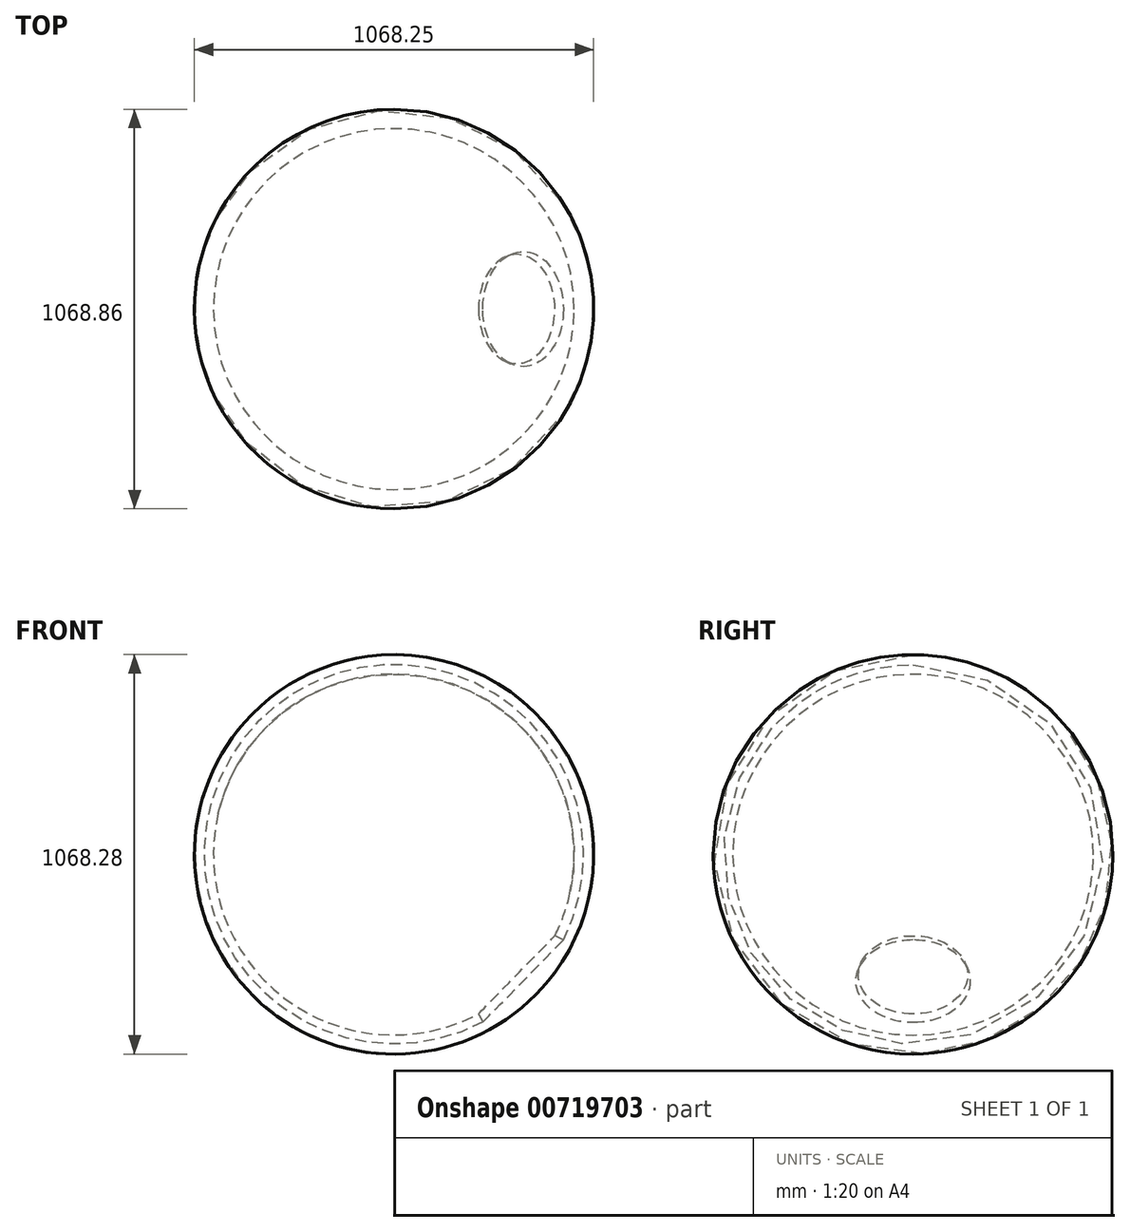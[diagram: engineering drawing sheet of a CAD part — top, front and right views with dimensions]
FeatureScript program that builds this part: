
annotation { "Feature Type Name" : "Feature", "Feature Type Description" : "" }
export const myFeature = defineFeature(function(context is Context, id is Id, definition is map)
    precondition{}
    {
        {
            var Q0;
            Q0=qCreatedBy(makeId("Front.planeOp"),FACE);
            var sketch = newSketch(context, id + "F0", { "sketchPlane" : qUnion([Q0])});
            skArc(sketch, "E0", {"start": v(469.78, -110.48) * mm, "mid": v(110.48, 469.78) * mm, "end": v(-469.78, 110.48) * mm});
            skLineSegment(sketch, "E1", {"start": v(469.78, -110.48) * mm, "end": v(0, 0) * mm});
            skLineSegment(sketch, "E2", {"start": v(0, 0) * mm, "end": v(-469.78, 110.48) * mm});
            skSolve(sketch);
        }
        {
            var Q0;
            Q0=makeQuery(id+"F0.imprint","IMPRINT",FACE,{"disambiguationData":[TD([[makeQuery(id+"F0.imprint","IMPRINT",EDGE,{"derivedFrom":sQuery(id+"F0.wireOp",EDGE,"E0")}),1.0]])]});
            var sketch = newSketch(context, id + "F1", { "sketchPlane" : qUnion([Q0])});
            skArc(sketch, "E3", {"start": v(453.81, -228.3) * mm, "mid": v(228.3, 453.81) * mm, "end": v(-453.81, 228.3) * mm});
            skLineSegment(sketch, "E4", {"start": v(0, 0) * mm, "end": v(453.81, -228.3) * mm});
            skLineSegment(sketch, "E5", {"start": v(453.81, -228.3) * mm, "end": v(-453.81, 228.3) * mm});
            skArc(sketch, "E6", {"start": v(381.43, -372.86) * mm, "mid": v(373.6, 380.7) * mm, "end": v(-379.98, 374.34) * mm});
            skLineSegment(sketch, "E7", {"start": v(0, 0) * mm, "end": v(381.43, -372.86) * mm});
            skLineSegment(sketch, "E8", {"start": v(381.43, -372.86) * mm, "end": v(-379.98, 374.34) * mm});
            skSolve(sketch);
        }
        {
            var Q0;
            Q0=makeQuery(id+"F0.imprint","IMPRINT",FACE,{"disambiguationData":[TD([[makeQuery(id+"F0.imprint","IMPRINT",EDGE,{"derivedFrom":sQuery(id+"F0.wireOp",EDGE,"E0")}),1.0]])]});
            var Q1;
            Q1=sQuery(id+"F0.wireOp",EDGE,"E2");
            revolve(context, id + "F2", {"surfaceOperationType" : NewSurfaceOperationType.NEW, "entities" : qUnion([Q0]), "axis" : qUnion([Q1]), "revolveType" : RevolveType.FULL});
        }
        {
            var Q0;
            {var subQ1=sQuery(id+"F1.wireOp",EDGE,"E6");Q0=makeQuery(id+"F1.imprint","IMPRINT",FACE,{"disambiguationData":[TD([[makeQuery(id+"F1.imprint","IMPRINT",EDGE,{"derivedFrom":subQ1}),1.0]])]});}
            var Q1;
            Q1=sQuery(id+"F1.wireOp",EDGE,"E8");
            revolve(context, id + "F3", {"operationType" : NewBodyOperationType.ADD, "surfaceOperationType" : NewSurfaceOperationType.NEW, "entities" : qUnion([Q0]), "axis" : qUnion([Q1]), "revolveType" : RevolveType.FULL});
        }
    });
